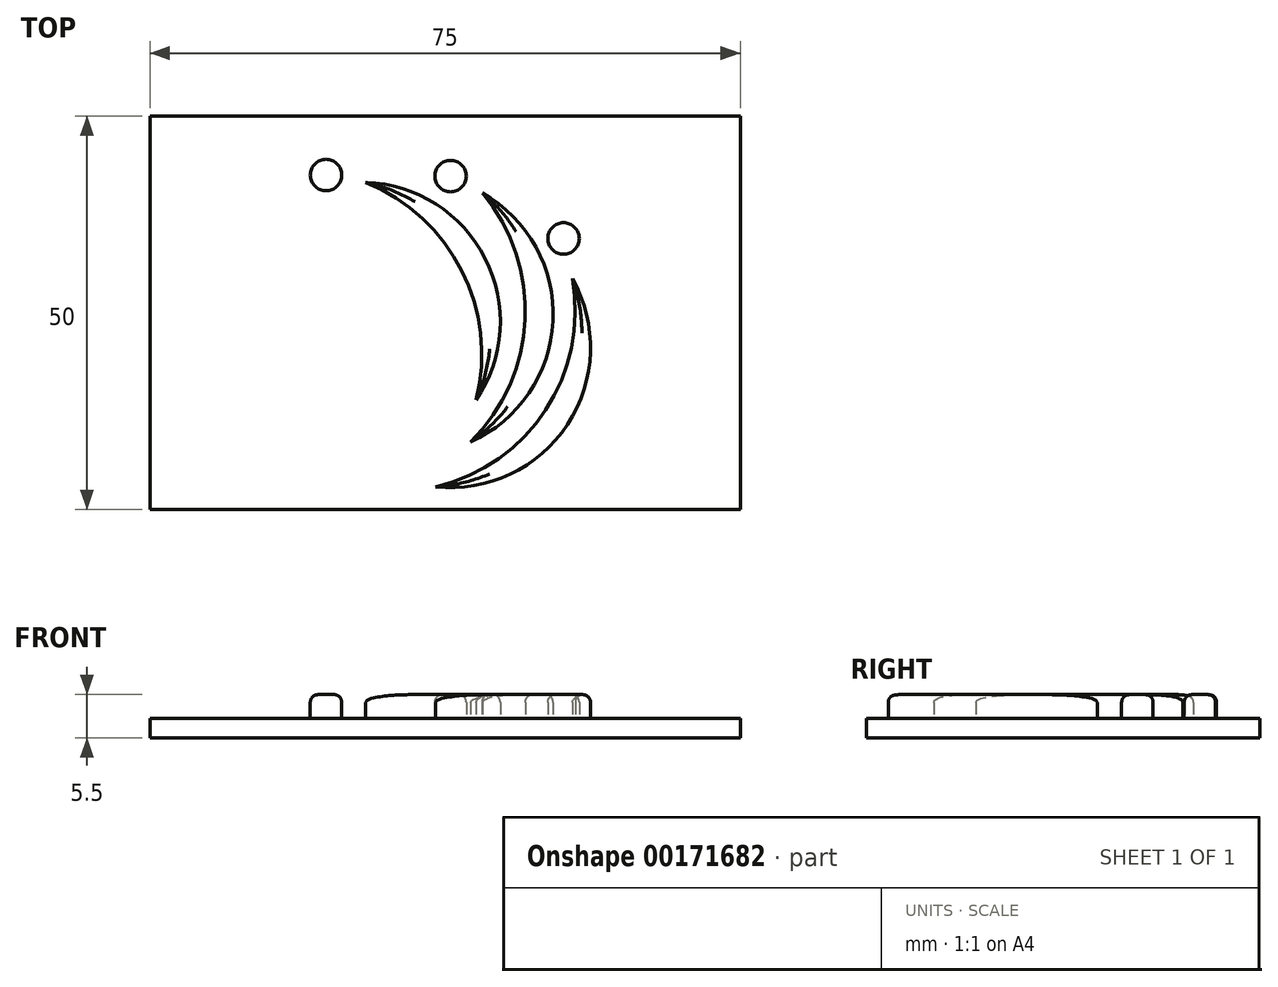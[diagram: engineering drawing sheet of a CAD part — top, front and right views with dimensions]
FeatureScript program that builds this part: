
annotation { "Feature Type Name" : "Feature", "Feature Type Description" : "" }
export const myFeature = defineFeature(function(context is Context, id is Id, definition is map)
    precondition{}
    {
        {
            var Q0;
            Q0=qCreatedBy(makeId("Top.planeOp"),FACE);
            var sketch = newSketch(context, id + "F0", { "sketchPlane" : qUnion([Q0])});
            skLineSegment(sketch, "E0.bottom", {"start": v(-37.5, 25) * mm, "end": v(37.5, 25) * mm});
            skLineSegment(sketch, "E0.top", {"start": v(-37.5, -25) * mm, "end": v(37.5, -25) * mm});
            skLineSegment(sketch, "E0.left", {"start": v(-37.5, 25) * mm, "end": v(-37.5, -25) * mm});
            skLineSegment(sketch, "E0.right", {"start": v(37.5, 25) * mm, "end": v(37.5, -25) * mm});
            skPoint(sketch, "E0.middle", {"position": v(0, 0) * mm});
            skSolve(sketch);
        }
        {
            var Q0;
            Q0 = qSketchRegion(id + "F0", true);
            extrude(context, id + "F1", {"entities" : qUnion([Q0]), "depth" : 2.5 * mm});
        }
        {
            var Q0;
            Q0=makeQuery(id+"F1.opExtrude","CAP_FACE",FACE,{"disambiguationData":[OSD([sQuery(id+"F0.wireOp",EDGE,"E0.bottom"),sQuery(id+"F0.wireOp",EDGE,"E0.top"),sQuery(id+"F0.wireOp",EDGE,"E0.left"),sQuery(id+"F0.wireOp",EDGE,"E0.right")])],"isStart":false});
            var sketch = newSketch(context, id + "F2", { "sketchPlane" : qUnion([Q0])});
            skArc(sketch, "E1", {"start": v(-1.2, -22.11) * mm, "mid": v(12.78, -12.35) * mm, "end": v(16.16, 4.37) * mm});
            skArc(sketch, "E2", {"start": v(-1.2, -22.11) * mm, "mid": v(15.55, -14.17) * mm, "end": v(16.16, 4.37) * mm});
            skArc(sketch, "E3", {"start": v(3.23, -16.4) * mm, "mid": v(10.17, -0.88) * mm, "end": v(4.74, 15.23) * mm});
            skArc(sketch, "E4", {"start": v(3.23, -16.4) * mm, "mid": v(13.7, -1.05) * mm, "end": v(4.74, 15.23) * mm});
            skArc(sketch, "E5", {"start": v(3.95, -11.1) * mm, "mid": v(2.1, 5.37) * mm, "end": v(-10.09, 16.58) * mm});
            skArc(sketch, "E6", {"start": v(3.95, -11.1) * mm, "mid": v(5.1, 6.89) * mm, "end": v(-10.09, 16.58) * mm});
            skCircle(sketch, "E7", {"center": v(-15.12, 17.5) * mm, "radius": 2 * mm});
            skCircle(sketch, "E8", {"center": v(0.7, 17.37) * mm, "radius": 2 * mm});
            skCircle(sketch, "E9", {"center": v(15.05, 9.44) * mm, "radius": 2 * mm});
            skSolve(sketch);
        }
        {
            var Q0;
            Q0 = qSketchRegion(id + "F2", true);
            extrude(context, id + "F3", {"entities" : qUnion([Q0]), "operationType" : NewBodyOperationType.ADD, "depth" : 3 * mm});
        }
        {
            var Q0;
            Q0=makeQuery(id+"F3.opExtrude","CAP_EDGE",EDGE,{"disambiguationData":[OSD([sQuery(id+"F2.wireOp",EDGE,"E7")])],"isStart":false});
            var Q1;
            Q1=makeQuery(id+"F3.opExtrude","CAP_EDGE",EDGE,{"disambiguationData":[OSD([sQuery(id+"F2.wireOp",EDGE,"E8")])],"isStart":false});
            var Q2;
            Q2=makeQuery(id+"F3.opExtrude","CAP_EDGE",EDGE,{"disambiguationData":[OSD([sQuery(id+"F2.wireOp",EDGE,"E9")])],"isStart":false});
            var Q3;
            Q3=makeQuery(id+"F3.opExtrude","CAP_EDGE",EDGE,{"disambiguationData":[OSD([sQuery(id+"F2.wireOp",EDGE,"E2")])],"isStart":false});
            var Q4;
            Q4=makeQuery(id+"F3.opExtrude","CAP_EDGE",EDGE,{"disambiguationData":[OSD([sQuery(id+"F2.wireOp",EDGE,"E1")])],"isStart":false});
            var Q5;
            Q5=makeQuery(id+"F3.opExtrude","CAP_EDGE",EDGE,{"disambiguationData":[OSD([sQuery(id+"F2.wireOp",EDGE,"E4")])],"isStart":false});
            var Q6;
            Q6=makeQuery(id+"F3.opExtrude","CAP_EDGE",EDGE,{"disambiguationData":[OSD([sQuery(id+"F2.wireOp",EDGE,"E3")])],"isStart":false});
            var Q7;
            Q7=makeQuery(id+"F3.opExtrude","CAP_EDGE",EDGE,{"disambiguationData":[OSD([sQuery(id+"F2.wireOp",EDGE,"E6")])],"isStart":false});
            var Q8;
            Q8=makeQuery(id+"F3.opExtrude","CAP_EDGE",EDGE,{"disambiguationData":[OSD([sQuery(id+"F2.wireOp",EDGE,"E5")])],"isStart":false});
            fillet(context, id + "F4", {"entities" : qUnion([Q0, Q1, Q2, Q3, Q4, Q5, Q6, Q7, Q8]), "radius" : 1 * mm, "tangentPropagation" : true, "allowEdgeOverflow" : false});
        }
    });
